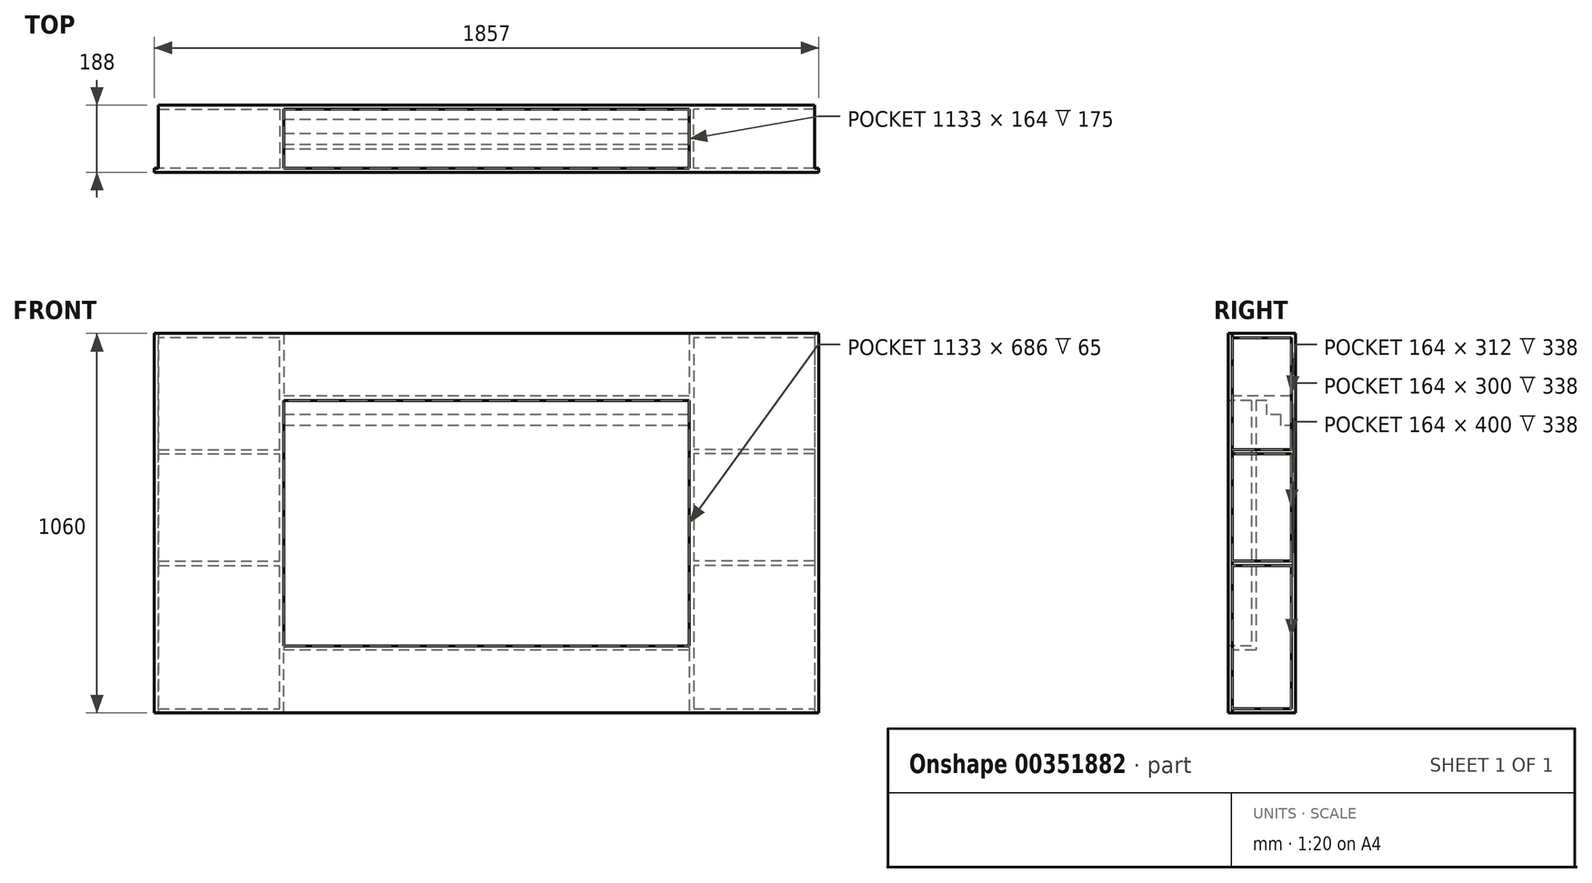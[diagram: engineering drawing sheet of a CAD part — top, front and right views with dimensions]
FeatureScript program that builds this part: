
annotation { "Feature Type Name" : "Feature", "Feature Type Description" : "" }
export const myFeature = defineFeature(function(context is Context, id is Id, definition is map)
    precondition{}
    {
        {
            var Q0;
            Q0=qCreatedBy(makeId("Front.planeOp"),FACE);
            var sketch = newSketch(context, id + "F0", { "sketchPlane" : qUnion([Q0])});
            skLineSegment(sketch, "E0.bottom", {"start": v(-900, 530) * mm, "end": v(900, 530) * mm});
            skLineSegment(sketch, "E0.top", {"start": v(-900, -530) * mm, "end": v(900, -530) * mm});
            skLineSegment(sketch, "E0.left", {"start": v(-900, 530) * mm, "end": v(-900, -530) * mm});
            skLineSegment(sketch, "E0.right", {"start": v(900, 530) * mm, "end": v(900, -530) * mm});
            skPoint(sketch, "E0.middle", {"position": v(0, 0) * mm});
            skSolve(sketch);
        }
        {
            var Q0;
            Q0 = qSketchRegion(id + "F0", true);
            extrude(context, id + "F1", {"entities" : qUnion([Q0]), "depth" : 12 * mm});
        }
        {
            var Q0;
            Q0=qCreatedBy(makeId("Front.planeOp"),FACE);
            cPlane(context, id + "F2", {"entities" : qUnion([Q0]), "cplaneType" : CPlaneType.OFFSET, "offset" : 176 * mm, "oppositeDirection" : true, "width" : 150 * mm, "height" : 150 * mm});
        }
        {
            var Q0;
            Q0=qCreatedBy(id+"F2.planeOp",FACE);
            var sketch = newSketch(context, id + "F3", { "sketchPlane" : qUnion([Q0])});
            skLineSegment(sketch, "E1.0", {"start": v(-900, 530) * mm, "end": v(-566.5, 530) * mm});
            skLineSegment(sketch, "E2", {"start": v(900, 518) * mm, "end": v(566.5, 518) * mm});
            skLineSegment(sketch, "E3", {"start": v(900, 530) * mm, "end": v(900, 518) * mm});
            skLineSegment(sketch, "E4", {"start": v(-900, 530) * mm, "end": v(-900, 518) * mm});
            skLineSegment(sketch, "E5", {"start": v(566.5, 530) * mm, "end": v(566.5, 518) * mm});
            skLineSegment(sketch, "E6", {"start": v(-566.5, 518) * mm, "end": v(-566.5, 530) * mm});
            skLineSegment(sketch, "E7.trimOffspring", {"start": v(-566.5, 518) * mm, "end": v(-900, 518) * mm});
            skLineSegment(sketch, "E8.trimOffspring", {"start": v(566.5, 530) * mm, "end": v(900, 530) * mm});
            skSolve(sketch);
        }
        {
            var Q0;
            Q0 = qSketchRegion(id + "F3", true);
            extrude(context, id + "F4", {"entities" : qUnion([Q0]), "operationType" : NewBodyOperationType.ADD, "endBound" : BoundingType.UP_TO_NEXT, "depth" : 25 * mm});
        }
        {
            var Q0;
            Q0=qCreatedBy(id+"F2.planeOp",FACE);
            var sketch = newSketch(context, id + "F5", { "sketchPlane" : qUnion([Q0])});
            skLineSegment(sketch, "E9", {"start": v(578.5, 518) * mm, "end": v(578.5, -518) * mm});
            skLineSegment(sketch, "E10", {"start": v(578.5, -518) * mm, "end": v(900, -518) * mm});
            skLineSegment(sketch, "E11", {"start": v(900, -518) * mm, "end": v(900, -530) * mm});
            skLineSegment(sketch, "E12", {"start": v(900, -530) * mm, "end": v(566.5, -530) * mm});
            skLineSegment(sketch, "E13", {"start": v(-900, -530) * mm, "end": v(-900, -518) * mm});
            skLineSegment(sketch, "E14", {"start": v(-900, -518) * mm, "end": v(-578.5, -518) * mm});
            skLineSegment(sketch, "E15", {"start": v(-578.5, -518) * mm, "end": v(-578.5, 518) * mm});
            skLineSegment(sketch, "E16", {"start": v(-578.5, 518) * mm, "end": v(-566.5, 518) * mm});
            skLineSegment(sketch, "E17", {"start": v(-566.5, 518) * mm, "end": v(-566.5, -530) * mm});
            skLineSegment(sketch, "E18", {"start": v(566.5, -530) * mm, "end": v(566.5, 518) * mm});
            skLineSegment(sketch, "E19", {"start": v(566.5, 518) * mm, "end": v(578.5, 518) * mm});
            skLineSegment(sketch, "E20.trimOffspring", {"start": v(-566.5, -530) * mm, "end": v(-900, -530) * mm});
            skSolve(sketch);
        }
        {
            var Q0;
            Q0 = qSketchRegion(id + "F5", true);
            extrude(context, id + "F6", {"entities" : qUnion([Q0]), "operationType" : NewBodyOperationType.ADD, "endBound" : BoundingType.UP_TO_NEXT, "depth" : 25 * mm});
        }
        {
            var Q0;
            Q0=qCreatedBy(makeId("Right.planeOp"),FACE);
            var sketch = newSketch(context, id + "F7", { "sketchPlane" : qUnion([Q0])});
            skLineSegment(sketch, "E21", {"start": v(176, 343) * mm, "end": v(176, 273) * mm});
            skLineSegment(sketch, "E22", {"start": v(176, 273) * mm, "end": v(136, 273) * mm});
            skLineSegment(sketch, "E23", {"start": v(136, 273) * mm, "end": v(136, 303) * mm});
            skLineSegment(sketch, "E24", {"start": v(136, 303) * mm, "end": v(96, 303) * mm});
            skLineSegment(sketch, "E25", {"start": v(96, 303) * mm, "end": v(96, 343) * mm});
            skLineSegment(sketch, "E26", {"start": v(96, 343) * mm, "end": v(176, 343) * mm});
            skSolve(sketch);
        }
        {
            var Q0;
            Q0 = qSketchRegion(id + "F7", true);
            extrude(context, id + "F8", {"entities" : qUnion([Q0]), "operationType" : NewBodyOperationType.ADD, "endBound" : BoundingType.UP_TO_NEXT, "depth" : 25 * mm, "hasSecondDirection" : true, "secondDirectionBound" : SecondDirectionBoundingType.UP_TO_NEXT, "secondDirectionOppositeDirection" : true, "secondDirectionDepth" : 25 * mm});
        }
        {
            var Q0;
            Q0=makeQuery(id+"F1.opExtrude","CAP_FACE",FACE,{"disambiguationData":[OSD([sQuery(id+"F0.wireOp",EDGE,"E0.bottom"),sQuery(id+"F0.wireOp",EDGE,"E0.top"),sQuery(id+"F0.wireOp",EDGE,"E0.left"),sQuery(id+"F0.wireOp",EDGE,"E0.right")])],"isStart":false});
            var sketch = newSketch(context, id + "F9", { "sketchPlane" : qUnion([Q0])});
            skLineSegment(sketch, "E27.bottom", {"start": v(-566.5, 343) * mm, "end": v(566.5, 343) * mm});
            skLineSegment(sketch, "E27.top", {"start": v(-566.5, -343) * mm, "end": v(566.5, -343) * mm});
            skLineSegment(sketch, "E27.left", {"start": v(-566.5, 343) * mm, "end": v(-566.5, -343) * mm});
            skLineSegment(sketch, "E27.right", {"start": v(566.5, 343) * mm, "end": v(566.5, -343) * mm});
            skSolve(sketch);
        }
        {
            var Q0;
            Q0=makeQuery(id+"F9.imprint","IMPRINT",FACE,{"disambiguationData":[TD([[makeQuery(id+"F9.imprint","IMPRINT",EDGE,{"derivedFrom":sQuery(id+"F9.wireOp",EDGE,"E27.bottom")}),-1.0]])]});
            extrude(context, id + "F10", {"entities" : qUnion([Q0]), "operationType" : NewBodyOperationType.REMOVE, "oppositeDirection" : true, "depth" : 25 * mm});
        }
        {
            var Q0;
            Q0=makeQuery(id+"F0.imprint","IMPRINT",FACE,{"disambiguationData":[TD([[makeQuery(id+"F0.imprint","IMPRINT",EDGE,{"derivedFrom":sQuery(id+"F0.wireOp",EDGE,"E0.bottom")}),-1.0]])]});
            var sketch = newSketch(context, id + "F11", { "sketchPlane" : qUnion([Q0])});
            skLineSegment(sketch, "E28.bottom", {"start": v(566.5, 355) * mm, "end": v(-566.5, 355) * mm});
            skLineSegment(sketch, "E28.top", {"start": v(566.5, 343) * mm, "end": v(-566.5, 343) * mm});
            skLineSegment(sketch, "E28.left", {"start": v(566.5, 355) * mm, "end": v(566.5, 343) * mm});
            skLineSegment(sketch, "E28.right", {"start": v(-566.5, 355) * mm, "end": v(-566.5, 343) * mm});
            skSolve(sketch);
        }
        {
            var Q0;
            Q0 = qSketchRegion(id + "F11", true);
            var Q1;
            Q1=makeQuery(id+"F8.boolean.opBoolean","MERGE",FACE,{"derivedFrom":[makeQuery(id+"F6.boolean.opBoolean","MERGE",FACE,{"derivedFrom":[makeQuery(id+"F4.opExtrude","CAP_FACE",FACE,{"disambiguationData":[OSD([sQuery(id+"F3.wireOp",EDGE,"E1.0"),sQuery(id+"F3.wireOp",EDGE,"E4"),sQuery(id+"F3.wireOp",EDGE,"E6"),sQuery(id+"F3.wireOp",EDGE,"E7.trimOffspring")])],"isStart":true}),makeQuery(id+"F6.opExtrude","CAP_FACE",FACE,{"disambiguationData":[OSD([sQuery(id+"F5.wireOp",EDGE,"E13"),sQuery(id+"F5.wireOp",EDGE,"E14"),sQuery(id+"F5.wireOp",EDGE,"E15"),sQuery(id+"F5.wireOp",EDGE,"E16"),sQuery(id+"F5.wireOp",EDGE,"E17"),sQuery(id+"F5.wireOp",EDGE,"E20.trimOffspring")])],"isStart":true})]}),makeQuery(id+"F6.boolean.opBoolean","MERGE",FACE,{"derivedFrom":[makeQuery(id+"F4.opExtrude","CAP_FACE",FACE,{"disambiguationData":[OSD([sQuery(id+"F3.wireOp",EDGE,"E2"),sQuery(id+"F3.wireOp",EDGE,"E3"),sQuery(id+"F3.wireOp",EDGE,"E5"),sQuery(id+"F3.wireOp",EDGE,"E8.trimOffspring")])],"isStart":true}),makeQuery(id+"F6.opExtrude","CAP_FACE",FACE,{"disambiguationData":[OSD([sQuery(id+"F5.wireOp",EDGE,"E9"),sQuery(id+"F5.wireOp",EDGE,"E10"),sQuery(id+"F5.wireOp",EDGE,"E11"),sQuery(id+"F5.wireOp",EDGE,"E12"),sQuery(id+"F5.wireOp",EDGE,"E18"),sQuery(id+"F5.wireOp",EDGE,"E19")])],"isStart":true})]}),makeQuery(id+"F8.opExtrude","SWEPT_FACE",FACE,{"disambiguationData":[OSD([sQuery(id+"F7.wireOp",EDGE,"E21")])]})]});
            extrude(context, id + "F12", {"entities" : qUnion([Q0]), "operationType" : NewBodyOperationType.ADD, "endBound" : BoundingType.UP_TO_SURFACE, "oppositeDirection" : true, "endBoundEntityFace" : qUnion([Q1]), "depth" : 80 * mm});
        }
        {
            var Q0;
            Q0=makeQuery(id+"F12.boolean.opBoolean","MERGE",FACE,{"derivedFrom":[makeQuery(id+"F8.boolean.opBoolean","MERGE",FACE,{"derivedFrom":[makeQuery(id+"F6.boolean.opBoolean","MERGE",FACE,{"derivedFrom":[makeQuery(id+"F4.opExtrude","CAP_FACE",FACE,{"disambiguationData":[OSD([sQuery(id+"F3.wireOp",EDGE,"E1.0"),sQuery(id+"F3.wireOp",EDGE,"E4"),sQuery(id+"F3.wireOp",EDGE,"E6"),sQuery(id+"F3.wireOp",EDGE,"E7.trimOffspring")])],"isStart":true}),makeQuery(id+"F6.opExtrude","CAP_FACE",FACE,{"disambiguationData":[OSD([sQuery(id+"F5.wireOp",EDGE,"E13"),sQuery(id+"F5.wireOp",EDGE,"E14"),sQuery(id+"F5.wireOp",EDGE,"E15"),sQuery(id+"F5.wireOp",EDGE,"E16"),sQuery(id+"F5.wireOp",EDGE,"E17"),sQuery(id+"F5.wireOp",EDGE,"E20.trimOffspring")])],"isStart":true})]}),makeQuery(id+"F6.boolean.opBoolean","MERGE",FACE,{"derivedFrom":[makeQuery(id+"F4.opExtrude","CAP_FACE",FACE,{"disambiguationData":[OSD([sQuery(id+"F3.wireOp",EDGE,"E2"),sQuery(id+"F3.wireOp",EDGE,"E3"),sQuery(id+"F3.wireOp",EDGE,"E5"),sQuery(id+"F3.wireOp",EDGE,"E8.trimOffspring")])],"isStart":true}),makeQuery(id+"F6.opExtrude","CAP_FACE",FACE,{"disambiguationData":[OSD([sQuery(id+"F5.wireOp",EDGE,"E9"),sQuery(id+"F5.wireOp",EDGE,"E10"),sQuery(id+"F5.wireOp",EDGE,"E11"),sQuery(id+"F5.wireOp",EDGE,"E12"),sQuery(id+"F5.wireOp",EDGE,"E18"),sQuery(id+"F5.wireOp",EDGE,"E19")])],"isStart":true})]}),makeQuery(id+"F8.opExtrude","SWEPT_FACE",FACE,{"disambiguationData":[OSD([sQuery(id+"F7.wireOp",EDGE,"E21")])]})]}),makeQuery(id+"F12.opExtrude","CAP_FACE",FACE,{"disambiguationData":[OSD([sQuery(id+"F11.wireOp",EDGE,"E28.bottom"),sQuery(id+"F11.wireOp",EDGE,"E28.top"),sQuery(id+"F11.wireOp",EDGE,"E28.left"),sQuery(id+"F11.wireOp",EDGE,"E28.right")])],"isStart":false})]});
            var sketch = newSketch(context, id + "F13", { "sketchPlane" : qUnion([Q0])});
            skLineSegment(sketch, "E29.0", {"start": v(-578.5, 518) * mm, "end": v(-578.5, 518) * mm});
            skLineSegment(sketch, "E30.0", {"start": v(578.5, -518) * mm, "end": v(578.5, 518) * mm});
            skLineSegment(sketch, "E31.0", {"start": v(900, -518) * mm, "end": v(578.5, -518) * mm});
            skLineSegment(sketch, "E32.0", {"start": v(-900, 518) * mm, "end": v(-578.5, 518) * mm});
            skLineSegment(sketch, "E33.0", {"start": v(-578.5, 518) * mm, "end": v(-578.5, -518) * mm});
            skLineSegment(sketch, "E34.0", {"start": v(-578.5, -518) * mm, "end": v(-900, -518) * mm});
            skLineSegment(sketch, "E35", {"start": v(-900, 518) * mm, "end": v(-900, -518) * mm});
            skLineSegment(sketch, "E36", {"start": v(900, -518) * mm, "end": v(900, 518) * mm});
            skLineSegment(sketch, "E37", {"start": v(900, 518) * mm, "end": v(578.5, 518) * mm});
            skSolve(sketch);
        }
        {
            var Q0;
            Q0 = qSketchRegion(id + "F13", true);
            extrude(context, id + "F14", {"entities" : qUnion([Q0]), "operationType" : NewBodyOperationType.ADD, "oppositeDirection" : true, "depth" : 12 * mm});
        }
        {
            var Q0;
            Q0=qCreatedBy(makeId("Top.planeOp"),FACE);
            var sketch = newSketch(context, id + "F15", { "sketchPlane" : qUnion([Q0])});
            skLineSegment(sketch, "E38.bottom", {"start": v(-566.5, 53) * mm, "end": v(566.5, 53) * mm});
            skLineSegment(sketch, "E38.top", {"start": v(-566.5, 65) * mm, "end": v(566.5, 65) * mm});
            skLineSegment(sketch, "E38.left", {"start": v(-566.5, 53) * mm, "end": v(-566.5, 65) * mm});
            skLineSegment(sketch, "E38.right", {"start": v(566.5, 53) * mm, "end": v(566.5, 65) * mm});
            skSolve(sketch);
        }
        {
            var Q0;
            Q0=makeQuery(id+"F15.imprint","IMPRINT",FACE,{"disambiguationData":[TD([[makeQuery(id+"F15.imprint","IMPRINT",EDGE,{"derivedFrom":sQuery(id+"F15.wireOp",EDGE,"E38.bottom")}),1.0]])]});
            var Q1;
            Q1=makeQuery(id+"F12.boolean.opBoolean","MERGE",FACE,{"derivedFrom":[makeQuery(id+"F10.boolean.opBoolean","COPY",FACE,{"derivedFrom":makeQuery(id+"F10.opExtrude","SWEPT_FACE",FACE,{"disambiguationData":[OSD([sQuery(id+"F9.wireOp",EDGE,"E27.bottom")])]})}),makeQuery(id+"F12.opExtrude","SWEPT_FACE",FACE,{"disambiguationData":[OSD([sQuery(id+"F11.wireOp",EDGE,"E28.top")])]})]});
            extrude(context, id + "F16", {"entities" : qUnion([Q0]), "operationType" : NewBodyOperationType.ADD, "endBound" : BoundingType.UP_TO_SURFACE, "endBoundEntityFace" : qUnion([Q1]), "depth" : 25 * mm});
        }
        {
            var Q0;
            Q0 = qSketchRegion(id + "F15", true);
            var Q1;
            Q1=makeQuery(id+"F10.boolean.opBoolean","COPY",FACE,{"derivedFrom":makeQuery(id+"F10.opExtrude","SWEPT_FACE",FACE,{"disambiguationData":[OSD([sQuery(id+"F9.wireOp",EDGE,"E27.top")])]})});
            extrude(context, id + "F17", {"entities" : qUnion([Q0]), "operationType" : NewBodyOperationType.ADD, "endBound" : BoundingType.UP_TO_SURFACE, "oppositeDirection" : true, "endBoundEntityFace" : qUnion([Q1]), "depth" : 400 * mm});
        }
        {
            var Q0;
            {var subQ3=sQuery(id+"F0.wireOp",EDGE,"E0.top");var subQ4=makeQuery(id+"F1.opExtrude","SWEPT_FACE",FACE,{"disambiguationData":[OSD([subQ3])]});var subQ8=sQuery(id+"F0.wireOp",EDGE,"E0.bottom");Q0=makeQuery(id+"F10.boolean.opBoolean","SPLIT",FACE,{"disambiguationData":[TD([subQ4])],"derivedFrom":makeQuery(id+"F6.boolean.opBoolean","SPLIT",FACE,{"disambiguationData":[TD([makeQuery(id+"F1.opExtrude","SWEPT_FACE",FACE,{"disambiguationData":[OSD([subQ8])]})])],"derivedFrom":makeQuery(id+"F1.opExtrude","CAP_FACE",FACE,{"disambiguationData":[OSD([subQ8,subQ3,sQuery(id+"F0.wireOp",EDGE,"E0.left"),sQuery(id+"F0.wireOp",EDGE,"E0.right")])],"isStart":true})})});}
            var sketch = newSketch(context, id + "F18", { "sketchPlane" : qUnion([Q0])});
            skLineSegment(sketch, "E39.bottom", {"start": v(-566.5, -343) * mm, "end": v(566.5, -343) * mm});
            skLineSegment(sketch, "E39.top", {"start": v(-566.5, -355) * mm, "end": v(566.5, -355) * mm});
            skLineSegment(sketch, "E39.left", {"start": v(-566.5, -343) * mm, "end": v(-566.5, -355) * mm});
            skLineSegment(sketch, "E39.right", {"start": v(566.5, -343) * mm, "end": v(566.5, -355) * mm});
            skSolve(sketch);
        }
        {
            var Q0;
            Q0=makeQuery(id+"F18.imprint","IMPRINT",FACE,{"disambiguationData":[TD([[makeQuery(id+"F18.imprint","IMPRINT",EDGE,{"derivedFrom":sQuery(id+"F18.wireOp",EDGE,"E39.bottom")}),1.0]])]});
            var Q1;
            {var subQ0=sQuery(id+"F15.wireOp",EDGE,"E38.top");Q1=makeQuery(id+"F17.boolean.opBoolean","MERGE",FACE,{"derivedFrom":[makeQuery(id+"F16.opExtrude","SWEPT_FACE",FACE,{"disambiguationData":[OSD([subQ0])]}),makeQuery(id+"F17.opExtrude","SWEPT_FACE",FACE,{"disambiguationData":[OSD([subQ0])]})]});}
            extrude(context, id + "F19", {"entities" : qUnion([Q0]), "operationType" : NewBodyOperationType.ADD, "endBound" : BoundingType.UP_TO_SURFACE, "endBoundEntityFace" : qUnion([Q1]), "depth" : 25 * mm});
        }
        {
            var Q0;
            {var subQ0=sQuery(id+"F15.wireOp",EDGE,"E38.bottom");Q0=makeQuery(id+"F17.boolean.opBoolean","MERGE",FACE,{"derivedFrom":[makeQuery(id+"F16.opExtrude","SWEPT_FACE",FACE,{"disambiguationData":[OSD([subQ0])]}),makeQuery(id+"F17.opExtrude","SWEPT_FACE",FACE,{"disambiguationData":[OSD([subQ0])]})]});}
            var sketch = newSketch(context, id + "F20", { "sketchPlane" : qUnion([Q0])});
            skLineSegment(sketch, "E40.bottom", {"start": v(-383.03, 117.62) * mm, "end": v(318.46, 117.62) * mm});
            skLineSegment(sketch, "E40.top", {"start": v(-383.03, -48.1) * mm, "end": v(318.46, -48.1) * mm});
            skLineSegment(sketch, "E40.left", {"start": v(-383.03, 117.62) * mm, "end": v(-383.03, -48.1) * mm});
            skLineSegment(sketch, "E40.right", {"start": v(318.46, 117.62) * mm, "end": v(318.46, -48.1) * mm});
            skSolve(sketch);
        }
        {
            var Q0;
            Q0=makeQuery(id+"F6.opExtrude","SWEPT_FACE",FACE,{"disambiguationData":[OSD([sQuery(id+"F5.wireOp",EDGE,"E15")])]});
            var sketch = newSketch(context, id + "F21", { "sketchPlane" : qUnion([Q0])});
            skLineSegment(sketch, "E41.bottom", {"start": v(-164, -106) * mm, "end": v(0, -106) * mm});
            skLineSegment(sketch, "E41.top", {"start": v(-164, -118) * mm, "end": v(0, -118) * mm});
            skLineSegment(sketch, "E41.left", {"start": v(-164, -106) * mm, "end": v(-164, -118) * mm});
            skLineSegment(sketch, "E41.right", {"start": v(0, -106) * mm, "end": v(0, -118) * mm});
            skLineSegment(sketch, "E42.bottom", {"start": v(-164, 206) * mm, "end": v(0, 206) * mm});
            skLineSegment(sketch, "E42.top", {"start": v(-164, 194) * mm, "end": v(0, 194) * mm});
            skLineSegment(sketch, "E42.left", {"start": v(-164, 206) * mm, "end": v(-164, 194) * mm});
            skLineSegment(sketch, "E42.right", {"start": v(0, 206) * mm, "end": v(0, 194) * mm});
            skSolve(sketch);
        }
        {
            var Q0;
            Q0 = qSketchRegion(id + "F21", true);
            var Q1;
            Q1=makeQuery(id+"F14.boolean.opBoolean","MERGE",FACE,{"derivedFrom":[makeQuery(id+"F6.boolean.opBoolean","MERGE",FACE,{"derivedFrom":[makeQuery(id+"F4.boolean.opBoolean","MERGE",FACE,{"derivedFrom":[makeQuery(id+"F1.opExtrude","SWEPT_FACE",FACE,{"disambiguationData":[OSD([sQuery(id+"F0.wireOp",EDGE,"E0.left")])]}),makeQuery(id+"F4.opExtrude","SWEPT_FACE",FACE,{"disambiguationData":[OSD([sQuery(id+"F3.wireOp",EDGE,"E4")])]})]}),makeQuery(id+"F6.opExtrude","SWEPT_FACE",FACE,{"disambiguationData":[OSD([sQuery(id+"F5.wireOp",EDGE,"E13")])]})]}),makeQuery(id+"F14.opExtrude","SWEPT_FACE",FACE,{"disambiguationData":[OSD([sQuery(id+"F13.wireOp",EDGE,"E36")])]})]});
            extrude(context, id + "F22", {"entities" : qUnion([Q0]), "operationType" : NewBodyOperationType.ADD, "endBound" : BoundingType.UP_TO_SURFACE, "endBoundEntityFace" : qUnion([Q1]), "depth" : 25 * mm});
        }
        {
            var Q0;
            Q0=makeQuery(id+"F6.opExtrude","SWEPT_FACE",FACE,{"disambiguationData":[OSD([sQuery(id+"F5.wireOp",EDGE,"E9")])]});
            var sketch = newSketch(context, id + "F23", { "sketchPlane" : qUnion([Q0])});
            skLineSegment(sketch, "E43.bottom", {"start": v(0, -106) * mm, "end": v(164, -106) * mm});
            skLineSegment(sketch, "E43.top", {"start": v(0, -118) * mm, "end": v(164, -118) * mm});
            skLineSegment(sketch, "E43.left", {"start": v(0, -106) * mm, "end": v(0, -118) * mm});
            skLineSegment(sketch, "E43.right", {"start": v(164, -106) * mm, "end": v(164, -118) * mm});
            skLineSegment(sketch, "E44.bottom", {"start": v(0, 206) * mm, "end": v(164, 206) * mm});
            skLineSegment(sketch, "E44.top", {"start": v(0, 194) * mm, "end": v(164, 194) * mm});
            skLineSegment(sketch, "E44.left", {"start": v(0, 206) * mm, "end": v(0, 194) * mm});
            skLineSegment(sketch, "E44.right", {"start": v(164, 206) * mm, "end": v(164, 194) * mm});
            skSolve(sketch);
        }
        {
            var Q0;
            Q0 = qSketchRegion(id + "F23", true);
            var Q1;
            Q1=makeQuery(id+"F14.boolean.opBoolean","MERGE",FACE,{"derivedFrom":[makeQuery(id+"F6.boolean.opBoolean","MERGE",FACE,{"derivedFrom":[makeQuery(id+"F4.boolean.opBoolean","MERGE",FACE,{"derivedFrom":[makeQuery(id+"F1.opExtrude","SWEPT_FACE",FACE,{"disambiguationData":[OSD([sQuery(id+"F0.wireOp",EDGE,"E0.right")])]}),makeQuery(id+"F4.opExtrude","SWEPT_FACE",FACE,{"disambiguationData":[OSD([sQuery(id+"F3.wireOp",EDGE,"E3")])]})]}),makeQuery(id+"F6.opExtrude","SWEPT_FACE",FACE,{"disambiguationData":[OSD([sQuery(id+"F5.wireOp",EDGE,"E11")])]})]}),makeQuery(id+"F14.opExtrude","SWEPT_FACE",FACE,{"disambiguationData":[OSD([sQuery(id+"F13.wireOp",EDGE,"E35")])]})]});
            extrude(context, id + "F24", {"entities" : qUnion([Q0]), "operationType" : NewBodyOperationType.ADD, "endBound" : BoundingType.UP_TO_SURFACE, "endBoundEntityFace" : qUnion([Q1]), "depth" : 25 * mm});
        }
        {
            var Q0;
            Q0=makeQuery(id+"F12.opExtrude","SWEPT_FACE",FACE,{"disambiguationData":[OSD([sQuery(id+"F11.wireOp",EDGE,"E28.bottom")])]});
            var sketch = newSketch(context, id + "F25", { "sketchPlane" : qUnion([Q0])});
            skLineSegment(sketch, "E45.bottom", {"start": v(566.5, 164) * mm, "end": v(-566.5, 164) * mm});
            skLineSegment(sketch, "E45.top", {"start": v(566.5, 176) * mm, "end": v(-566.5, 176) * mm});
            skLineSegment(sketch, "E45.left", {"start": v(566.5, 164) * mm, "end": v(566.5, 176) * mm});
            skLineSegment(sketch, "E45.right", {"start": v(-566.5, 164) * mm, "end": v(-566.5, 176) * mm});
            skSolve(sketch);
        }
        {
            var Q0;
            Q0 = qSketchRegion(id + "F25", true);
            var Q1;
            Q1=makeQuery(id+"F4.boolean.opBoolean","MERGE",FACE,{"derivedFrom":[makeQuery(id+"F1.opExtrude","SWEPT_FACE",FACE,{"disambiguationData":[OSD([sQuery(id+"F0.wireOp",EDGE,"E0.bottom")])]}),makeQuery(id+"F4.opExtrude","SWEPT_FACE",FACE,{"disambiguationData":[OSD([sQuery(id+"F3.wireOp",EDGE,"E1.0")])]}),makeQuery(id+"F4.opExtrude","SWEPT_FACE",FACE,{"disambiguationData":[OSD([sQuery(id+"F3.wireOp",EDGE,"E8.trimOffspring")])]})]});
            extrude(context, id + "F26", {"entities" : qUnion([Q0]), "operationType" : NewBodyOperationType.ADD, "endBound" : BoundingType.UP_TO_SURFACE, "endBoundEntityFace" : qUnion([Q1]), "depth" : 25 * mm});
        }
        {
            var Q0;
            Q0=makeQuery(id+"F22.boolean.opBoolean","MERGE",FACE,{"derivedFrom":[makeQuery(id+"F14.boolean.opBoolean","MERGE",FACE,{"derivedFrom":[makeQuery(id+"F6.boolean.opBoolean","MERGE",FACE,{"derivedFrom":[makeQuery(id+"F4.boolean.opBoolean","MERGE",FACE,{"derivedFrom":[makeQuery(id+"F1.opExtrude","SWEPT_FACE",FACE,{"disambiguationData":[OSD([sQuery(id+"F0.wireOp",EDGE,"E0.left")])]}),makeQuery(id+"F4.opExtrude","SWEPT_FACE",FACE,{"disambiguationData":[OSD([sQuery(id+"F3.wireOp",EDGE,"E4")])]})]}),makeQuery(id+"F6.opExtrude","SWEPT_FACE",FACE,{"disambiguationData":[OSD([sQuery(id+"F5.wireOp",EDGE,"E13")])]})]}),makeQuery(id+"F14.opExtrude","SWEPT_FACE",FACE,{"disambiguationData":[OSD([sQuery(id+"F13.wireOp",EDGE,"E36")])]})]}),makeQuery(id+"F22.opExtrude","CAP_FACE",FACE,{"disambiguationData":[OSD([sQuery(id+"F21.wireOp",EDGE,"E41.bottom"),sQuery(id+"F21.wireOp",EDGE,"E41.top"),sQuery(id+"F21.wireOp",EDGE,"E41.left"),sQuery(id+"F21.wireOp",EDGE,"E41.right")])],"isStart":false}),makeQuery(id+"F22.opExtrude","CAP_FACE",FACE,{"disambiguationData":[OSD([sQuery(id+"F21.wireOp",EDGE,"E42.bottom"),sQuery(id+"F21.wireOp",EDGE,"E42.top"),sQuery(id+"F21.wireOp",EDGE,"E42.left"),sQuery(id+"F21.wireOp",EDGE,"E42.right")])],"isStart":false})]});
            var sketch = newSketch(context, id + "F27", { "sketchPlane" : qUnion([Q0])});
            skLineSegment(sketch, "E46.bottom", {"start": v(12, 530) * mm, "end": v(0, 530) * mm});
            skLineSegment(sketch, "E46.top", {"start": v(12, -530) * mm, "end": v(0, -530) * mm});
            skLineSegment(sketch, "E46.left", {"start": v(12, 530) * mm, "end": v(12, -530) * mm});
            skLineSegment(sketch, "E46.right", {"start": v(0, 530) * mm, "end": v(0, -530) * mm});
            skSolve(sketch);
        }
        {
            var Q0;
            Q0 = qSketchRegion(id + "F27", true);
            extrude(context, id + "F28", {"entities" : qUnion([Q0]), "operationType" : NewBodyOperationType.ADD, "depth" : 28.5 * mm});
        }
        {
            var Q0;
            Q0=makeQuery(id+"F24.boolean.opBoolean","MERGE",FACE,{"derivedFrom":[makeQuery(id+"F14.boolean.opBoolean","MERGE",FACE,{"derivedFrom":[makeQuery(id+"F6.boolean.opBoolean","MERGE",FACE,{"derivedFrom":[makeQuery(id+"F4.boolean.opBoolean","MERGE",FACE,{"derivedFrom":[makeQuery(id+"F1.opExtrude","SWEPT_FACE",FACE,{"disambiguationData":[OSD([sQuery(id+"F0.wireOp",EDGE,"E0.right")])]}),makeQuery(id+"F4.opExtrude","SWEPT_FACE",FACE,{"disambiguationData":[OSD([sQuery(id+"F3.wireOp",EDGE,"E3")])]})]}),makeQuery(id+"F6.opExtrude","SWEPT_FACE",FACE,{"disambiguationData":[OSD([sQuery(id+"F5.wireOp",EDGE,"E11")])]})]}),makeQuery(id+"F14.opExtrude","SWEPT_FACE",FACE,{"disambiguationData":[OSD([sQuery(id+"F13.wireOp",EDGE,"E35")])]})]}),makeQuery(id+"F24.opExtrude","CAP_FACE",FACE,{"disambiguationData":[OSD([sQuery(id+"F23.wireOp",EDGE,"E43.bottom"),sQuery(id+"F23.wireOp",EDGE,"E43.top"),sQuery(id+"F23.wireOp",EDGE,"E43.left"),sQuery(id+"F23.wireOp",EDGE,"E43.right")])],"isStart":false}),makeQuery(id+"F24.opExtrude","CAP_FACE",FACE,{"disambiguationData":[OSD([sQuery(id+"F23.wireOp",EDGE,"E44.bottom"),sQuery(id+"F23.wireOp",EDGE,"E44.top"),sQuery(id+"F23.wireOp",EDGE,"E44.left"),sQuery(id+"F23.wireOp",EDGE,"E44.right")])],"isStart":false})]});
            var sketch = newSketch(context, id + "F29", { "sketchPlane" : qUnion([Q0])});
            skLineSegment(sketch, "E47.bottom", {"start": v(0, 530) * mm, "end": v(-12, 530) * mm});
            skLineSegment(sketch, "E47.top", {"start": v(0, -530) * mm, "end": v(-12, -530) * mm});
            skLineSegment(sketch, "E47.left", {"start": v(0, 530) * mm, "end": v(0, -530) * mm});
            skLineSegment(sketch, "E47.right", {"start": v(-12, 530) * mm, "end": v(-12, -530) * mm});
            skSolve(sketch);
        }
        {
            var Q0;
            Q0 = qSketchRegion(id + "F29", true);
            extrude(context, id + "F30", {"entities" : qUnion([Q0]), "operationType" : NewBodyOperationType.ADD, "depth" : 28.5 * mm});
        }
        {
            var Q0;
            Q0=makeQuery(id+"F24.boolean.opBoolean","MERGE",FACE,{"derivedFrom":[makeQuery(id+"F14.boolean.opBoolean","MERGE",FACE,{"derivedFrom":[makeQuery(id+"F6.boolean.opBoolean","MERGE",FACE,{"derivedFrom":[makeQuery(id+"F4.boolean.opBoolean","MERGE",FACE,{"derivedFrom":[makeQuery(id+"F1.opExtrude","SWEPT_FACE",FACE,{"disambiguationData":[OSD([sQuery(id+"F0.wireOp",EDGE,"E0.right")])]}),makeQuery(id+"F4.opExtrude","SWEPT_FACE",FACE,{"disambiguationData":[OSD([sQuery(id+"F3.wireOp",EDGE,"E3")])]})]}),makeQuery(id+"F6.opExtrude","SWEPT_FACE",FACE,{"disambiguationData":[OSD([sQuery(id+"F5.wireOp",EDGE,"E11")])]})]}),makeQuery(id+"F14.opExtrude","SWEPT_FACE",FACE,{"disambiguationData":[OSD([sQuery(id+"F13.wireOp",EDGE,"E35")])]})]}),makeQuery(id+"F24.opExtrude","CAP_FACE",FACE,{"disambiguationData":[OSD([sQuery(id+"F23.wireOp",EDGE,"E43.bottom"),sQuery(id+"F23.wireOp",EDGE,"E43.top"),sQuery(id+"F23.wireOp",EDGE,"E43.left"),sQuery(id+"F23.wireOp",EDGE,"E43.right")])],"isStart":false}),makeQuery(id+"F24.opExtrude","CAP_FACE",FACE,{"disambiguationData":[OSD([sQuery(id+"F23.wireOp",EDGE,"E44.bottom"),sQuery(id+"F23.wireOp",EDGE,"E44.top"),sQuery(id+"F23.wireOp",EDGE,"E44.left"),sQuery(id+"F23.wireOp",EDGE,"E44.right")])],"isStart":false})]});
            extrude(context, id + "F31", {"entities" : qUnion([Q0]), "operationType" : NewBodyOperationType.ADD, "depth" : 16.5 * mm});
        }
        {
            var Q0;
            Q0=makeQuery(id+"F22.boolean.opBoolean","MERGE",FACE,{"derivedFrom":[makeQuery(id+"F14.boolean.opBoolean","MERGE",FACE,{"derivedFrom":[makeQuery(id+"F6.boolean.opBoolean","MERGE",FACE,{"derivedFrom":[makeQuery(id+"F4.boolean.opBoolean","MERGE",FACE,{"derivedFrom":[makeQuery(id+"F1.opExtrude","SWEPT_FACE",FACE,{"disambiguationData":[OSD([sQuery(id+"F0.wireOp",EDGE,"E0.left")])]}),makeQuery(id+"F4.opExtrude","SWEPT_FACE",FACE,{"disambiguationData":[OSD([sQuery(id+"F3.wireOp",EDGE,"E4")])]})]}),makeQuery(id+"F6.opExtrude","SWEPT_FACE",FACE,{"disambiguationData":[OSD([sQuery(id+"F5.wireOp",EDGE,"E13")])]})]}),makeQuery(id+"F14.opExtrude","SWEPT_FACE",FACE,{"disambiguationData":[OSD([sQuery(id+"F13.wireOp",EDGE,"E36")])]})]}),makeQuery(id+"F22.opExtrude","CAP_FACE",FACE,{"disambiguationData":[OSD([sQuery(id+"F21.wireOp",EDGE,"E41.bottom"),sQuery(id+"F21.wireOp",EDGE,"E41.top"),sQuery(id+"F21.wireOp",EDGE,"E41.left"),sQuery(id+"F21.wireOp",EDGE,"E41.right")])],"isStart":false}),makeQuery(id+"F22.opExtrude","CAP_FACE",FACE,{"disambiguationData":[OSD([sQuery(id+"F21.wireOp",EDGE,"E42.bottom"),sQuery(id+"F21.wireOp",EDGE,"E42.top"),sQuery(id+"F21.wireOp",EDGE,"E42.left"),sQuery(id+"F21.wireOp",EDGE,"E42.right")])],"isStart":false})]});
            extrude(context, id + "F32", {"entities" : qUnion([Q0]), "operationType" : NewBodyOperationType.ADD, "depth" : 16.5 * mm});
        }
    });
